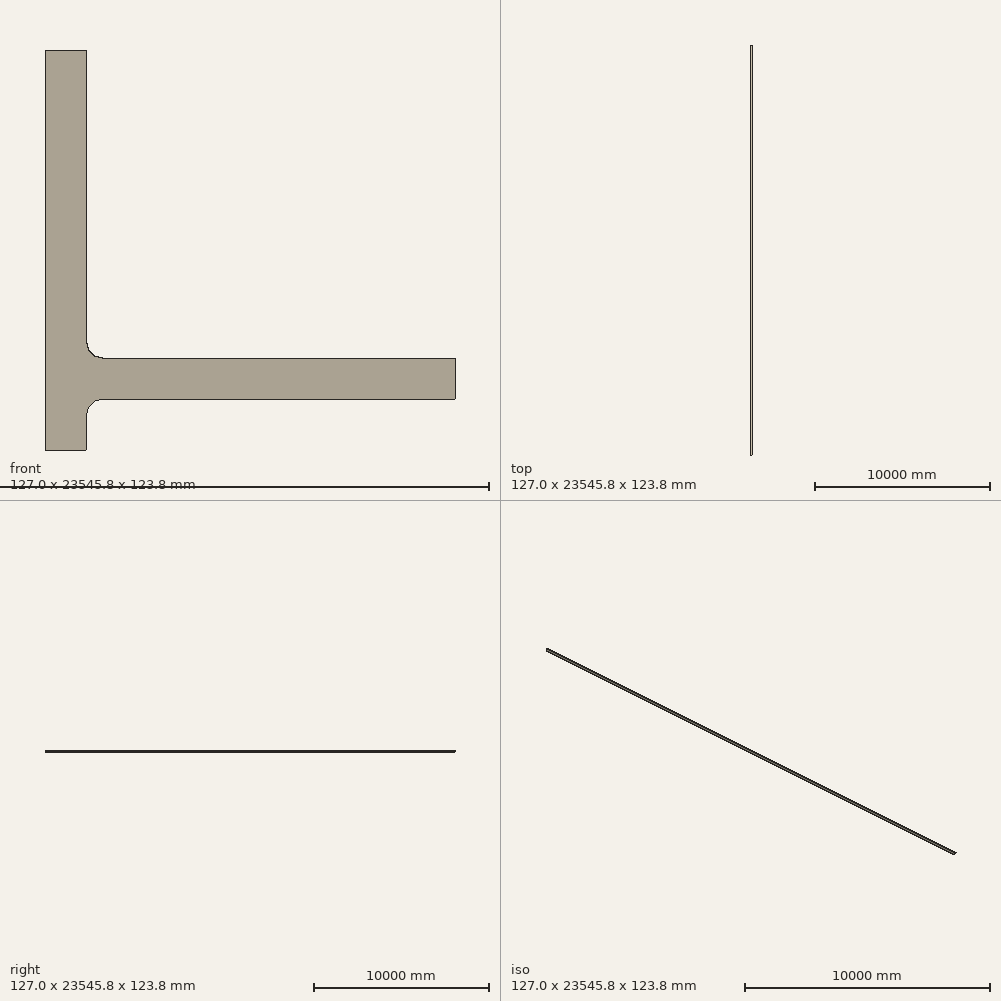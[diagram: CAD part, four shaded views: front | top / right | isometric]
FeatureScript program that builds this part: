
annotation { "Feature Type Name" : "Feature", "Feature Type Description" : "" }
export const myFeature = defineFeature(function(context is Context, id is Id, definition is map)
    precondition{}
    {
        {
            var Q0;
            Q0=qCreatedBy(makeId("Front.planeOp"),FACE);
            var sketch = newSketch(context, id + "F0", { "sketchPlane" : qUnion([Q0])});
            skLineSegment(sketch, "E0", {"start": v(0, 0) * mm, "end": v(0, 123.83) * mm});
            skLineSegment(sketch, "E1", {"start": v(0, 123.83) * mm, "end": v(12.7, 123.83) * mm});
            skLineSegment(sketch, "E2", {"start": v(12.7, 123.83) * mm, "end": v(12.7, 28.58) * mm});
            skLineSegment(sketch, "E3", {"start": v(12.7, 28.58) * mm, "end": v(127, 28.58) * mm});
            skLineSegment(sketch, "E4", {"start": v(127, 28.58) * mm, "end": v(127, 15.88) * mm});
            skLineSegment(sketch, "E5", {"start": v(127, 15.88) * mm, "end": v(12.7, 15.87) * mm});
            skLineSegment(sketch, "E6", {"start": v(12.7, 15.87) * mm, "end": v(12.7, 0) * mm});
            skLineSegment(sketch, "E7", {"start": v(12.7, 0) * mm, "end": v(0, 0) * mm});
            skLineSegment(sketch, "E8", {"start": v(0, 0) * mm, "end": v(0, 0) * mm});
            skLineSegment(sketch, "E9", {"start": v(127, 22.23) * mm, "end": v(0, 22.22) * mm, "construction": true});
            skSolve(sketch);
        }
        {
            var Q0;
            Q0=makeQuery(id+"F0.imprint","IMPRINT",FACE,{"disambiguationData":[TD([[makeQuery(id+"F0.imprint","IMPRINT",EDGE,{"derivedFrom":sQuery(id+"F0.wireOp",EDGE,"E0")}),-1.0]])]});
            extrude(context, id + "F1", {"entities" : qUnion([Q0]), "depth" : 23545.8 * mm, "offsetDistance" : 25.4 * mm});
        }
        {
            var Q0;
            Q0=makeQuery(id+"F1.opExtrude","SWEPT_EDGE",EDGE,{"disambiguationData":[OSD([sQuery(id+"F0.wireOp",EDGE,"E5"),sQuery(id+"F0.wireOp",EDGE,"E6")])]});
            fillet(context, id + "F2", {"entities" : qUnion([Q0]), "radius" : 5.08 * mm, "tangentPropagation" : true, "allowEdgeOverflow" : false});
        }
        {
            var Q0;
            Q0=makeQuery(id+"F1.opExtrude","SWEPT_EDGE",EDGE,{"disambiguationData":[OSD([sQuery(id+"F0.wireOp",EDGE,"E2"),sQuery(id+"F0.wireOp",EDGE,"E3")])]});
            fillet(context, id + "F3", {"entities" : qUnion([Q0]), "radius" : 5.08 * mm, "tangentPropagation" : true, "allowEdgeOverflow" : false});
        }
    });
